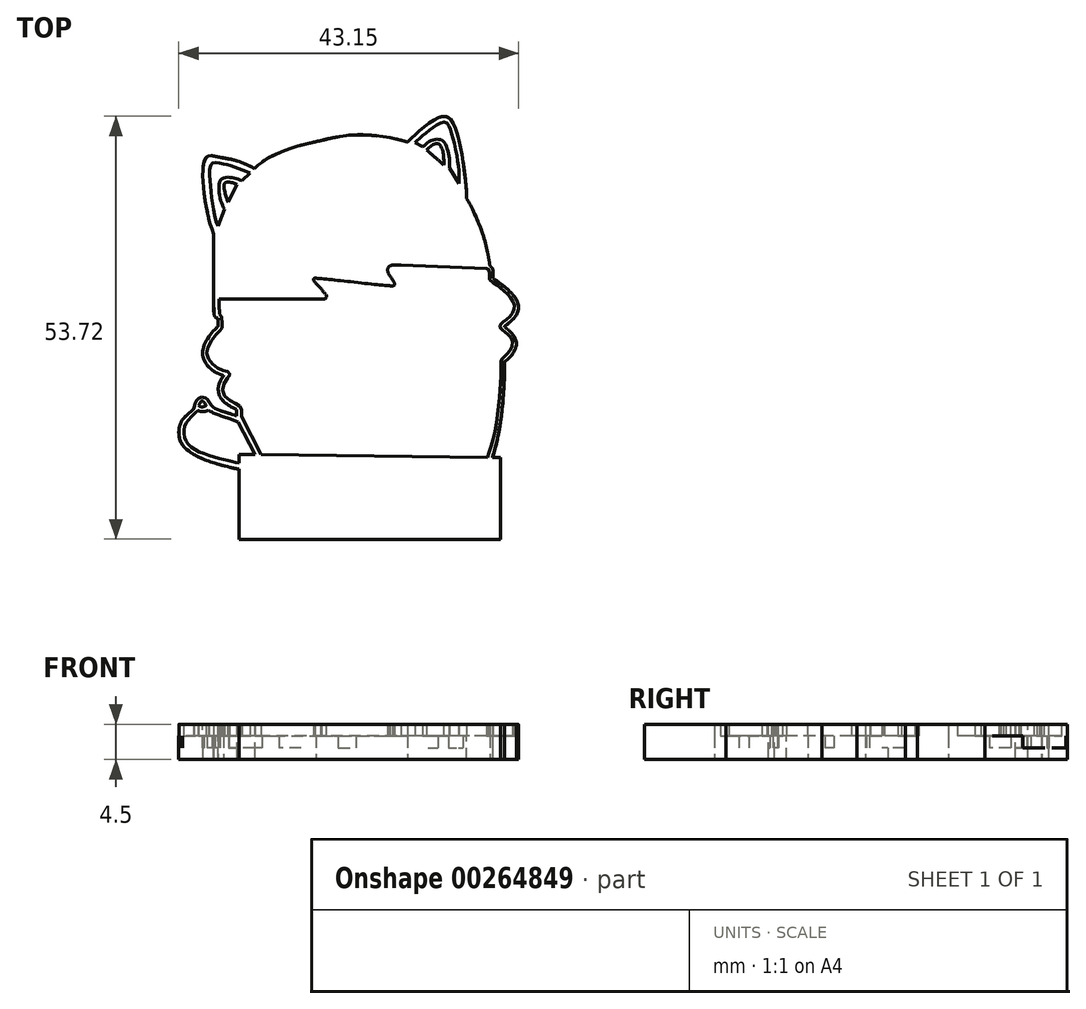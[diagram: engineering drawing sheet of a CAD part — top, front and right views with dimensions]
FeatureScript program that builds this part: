
annotation { "Feature Type Name" : "Feature", "Feature Type Description" : "" }
export const myFeature = defineFeature(function(context is Context, id is Id, definition is map)
    precondition{}
    {
        {
            var Q0;
            Q0=qCreatedBy(makeId("Top.planeOp"),FACE);
            var sketch = newSketch(context, id + "F0", { "sketchPlane" : qUnion([Q0])});
            skFitSpline(sketch, "E0", {"points": [v(-4.71, 21.15) * mm, v(-1.43, 21.85) * mm, v(2.13, 21.99) * mm, v(6.91, 21.1) * mm], "startDerivative": vector(9.73, 2.51) * mm, "endDerivative": vector(9.57, -3.47) * mm});
            skFitSpline(sketch, "E1", {"points": [v(6.91, 21.1) * mm, v(8.61, 22.68) * mm, v(10.2, 23.86) * mm, v(11.92, 24.32) * mm, v(13.1, 22.58) * mm, v(13.82, 19.54) * mm, v(14.44, 13.93) * mm], "startDerivative": vector(10.14, 10.11) * mm, "endDerivative": vector(0.67, -28.32) * mm});
            skFitSpline(sketch, "E2", {"points": [v(14.44, 13.93) * mm, v(15.56, 11.75) * mm, v(16.78, 8.45) * mm, v(17.4, 5.36) * mm], "startDerivative": vector(3.7, -6.8) * mm, "endDerivative": vector(1.45, -8.92) * mm});
            skFitSpline(sketch, "E3", {"points": [v(17.4, 5.36) * mm, v(17.73, 5.01) * mm, v(17.81, 4.5) * mm, v(17.81, 3.8) * mm], "startDerivative": vector(1.74, -1.34) * mm, "endDerivative": vector(0, -1.77) * mm});
            skFitSpline(sketch, "E4", {"points": [v(17.81, 3.8) * mm, v(19.4, 2.59) * mm, v(20.85, 0.9) * mm, v(20.85, -0.67) * mm, v(19.23, -2.33) * mm], "startDerivative": vector(6.54, -4.55) * mm, "endDerivative": vector(-7.42, -5.9) * mm});
            skFitSpline(sketch, "E5", {"points": [v(19.23, -2.33) * mm, v(20.06, -3.07) * mm, v(20.76, -4.46) * mm, v(20.23, -5.87) * mm, v(19.72, -6.4) * mm, v(19.25, -6.8) * mm], "startDerivative": vector(3.94, -3.89) * mm, "endDerivative": vector(-1.7, -1.2) * mm});
            skFitSpline(sketch, "E6", {"points": [v(19.25, -6.8) * mm, v(19.25, -8.45) * mm, v(18.85, -13.72) * mm, v(18.26, -16.97) * mm, v(17.71, -18.96) * mm], "startDerivative": vector(0.22, -7.28) * mm, "endDerivative": vector(-3.1, -9.32) * mm});
            skFitSpline(sketch, "E7", {"points": [v(-4.71, 21.15) * mm, v(-6.69, 20.68) * mm, v(-9.12, 19.83) * mm, v(-11.15, 18.86) * mm, v(-12.47, 17.72) * mm], "startDerivative": vector(-7.9, -1.66) * mm, "endDerivative": vector(-5.4, -5.31) * mm});
            skFitSpline(sketch, "E8", {"points": [v(-12.47, 17.72) * mm, v(-14.84, 18.75) * mm, v(-17.4, 19.25) * mm, v(-18.62, 19.2) * mm, v(-19.07, 16.98) * mm, v(-18.62, 12.76) * mm, v(-17.7, 9.27) * mm], "startDerivative": vector(-13.9, 7.08) * mm, "endDerivative": vector(5.2, -17.3) * mm});
            skFitSpline(sketch, "E9", {"points": [v(-17.7, 9.27) * mm, v(-17.7, 3.92) * mm, v(-17.7, 1.58) * mm], "startDerivative": vector(0, -9.8) * mm, "endDerivative": vector(0, -5.28) * mm});
            skFitSpline(sketch, "E10", {"points": [v(-17.7, 1.58) * mm, v(-17.7, -0.27) * mm, v(-17.48, -1.15) * mm, v(-17.12, -1.27) * mm], "startDerivative": vector(-0.1, -4.19) * mm, "endDerivative": vector(1.9, -0.2) * mm});
            skFitSpline(sketch, "E11", {"points": [v(-17.12, -1.27) * mm, v(-17.12, -2.27) * mm], "startDerivative": vector(0, -1) * mm, "endDerivative": vector(0, -1) * mm});
            skFitSpline(sketch, "E12", {"points": [v(-17.12, -2.27) * mm, v(-17.94, -3.16) * mm, v(-18.85, -4.56) * mm, v(-19, -6.33) * mm, v(-17.77, -7.93) * mm, v(-16.43, -8.56) * mm], "startDerivative": vector(-4.65, -4.51) * mm, "endDerivative": vector(7.01, -2.37) * mm});
            skFitSpline(sketch, "E13", {"points": [v(-16.43, -8.56) * mm, v(-16.98, -9.54) * mm, v(-17.1, -10.55) * mm, v(-16.7, -11.55) * mm, v(-15.79, -12.33) * mm, v(-14.77, -12.9) * mm], "startDerivative": vector(-2.9, -4.58) * mm, "endDerivative": vector(3.19, -2.1) * mm});
            skFitSpline(sketch, "E14", {"points": [v(-14.77, -12.9) * mm, v(-14.77, -13.67) * mm], "startDerivative": vector(0, -0.77) * mm, "endDerivative": vector(0, -0.77) * mm});
            skFitSpline(sketch, "E15", {"points": [v(-14.77, -13.67) * mm, v(-16.26, -13.2) * mm, v(-17.76, -12.58) * mm, v(-18.4, -11.72) * mm, v(-19.08, -11.3) * mm, v(-19.79, -11.63) * mm, v(-20.11, -12.33) * mm, v(-20.24, -12.76) * mm, v(-21.55, -14.05) * mm, v(-22.12, -15.73) * mm, v(-21.73, -17.26) * mm, v(-20.45, -18.43) * mm, v(-18.29, -19.45) * mm, v(-15.98, -20.12) * mm, v(-14.46, -20.43) * mm], "startDerivative": vector(-16.97, 4.2) * mm, "endDerivative": vector(20.47, -2.36) * mm});
            skLineSegment(sketch, "E16", {"start": v(-14.46, -20.43) * mm, "end": v(-14.46, -29.34) * mm});
            skLineSegment(sketch, "E17", {"start": v(-14.46, -29.34) * mm, "end": v(18.77, -29.34) * mm});
            skLineSegment(sketch, "E18", {"start": v(18.77, -29.34) * mm, "end": v(18.77, -18.96) * mm});
            skLineSegment(sketch, "E19", {"start": v(18.77, -18.96) * mm, "end": v(17.71, -18.96) * mm});
            skSolve(sketch);
        }
        {
            var Q0;
            Q0 = qSketchRegion(id + "F0", true);
            extrude(context, id + "F1", {"entities" : qUnion([Q0]), "depth" : 3 * mm, "offsetDistance" : 25 * mm});
        }
        {
            var Q0;
            Q0=makeQuery(id+"F1.opExtrude","CAP_FACE",FACE,{"disambiguationData":[OSD([sQuery(id+"F0.wireOp",EDGE,"E0"),sQuery(id+"F0.wireOp",EDGE,"E1"),sQuery(id+"F0.wireOp",EDGE,"E2"),sQuery(id+"F0.wireOp",EDGE,"E3"),sQuery(id+"F0.wireOp",EDGE,"E4"),sQuery(id+"F0.wireOp",EDGE,"E5"),sQuery(id+"F0.wireOp",EDGE,"E6"),sQuery(id+"F0.wireOp",EDGE,"E7"),sQuery(id+"F0.wireOp",EDGE,"E8"),sQuery(id+"F0.wireOp",EDGE,"E9"),sQuery(id+"F0.wireOp",EDGE,"E10"),sQuery(id+"F0.wireOp",EDGE,"E11"),sQuery(id+"F0.wireOp",EDGE,"E12"),sQuery(id+"F0.wireOp",EDGE,"E13"),sQuery(id+"F0.wireOp",EDGE,"E14"),sQuery(id+"F0.wireOp",EDGE,"E15"),sQuery(id+"F0.wireOp",EDGE,"E16"),sQuery(id+"F0.wireOp",EDGE,"E17"),sQuery(id+"F0.wireOp",EDGE,"E18"),sQuery(id+"F0.wireOp",EDGE,"E19")])],"isStart":false});
            var sketch = newSketch(context, id + "F2", { "sketchPlane" : qUnion([Q0])});
            skFitSpline(sketch, "E20", {"points": [v(6.91, 21.1) * mm, v(8.72, 22.77) * mm, v(10.83, 24.18) * mm, v(12.13, 24.22) * mm, v(13.15, 22.42) * mm, v(13.97, 18.7) * mm, v(14.4, 14.87) * mm, v(14.44, 13.93) * mm], "startDerivative": vector(11.52, 11.3) * mm, "endDerivative": vector(0.21, -7.73) * mm});
            skFitSpline(sketch, "E21", {"points": [v(8.86, 20.52) * mm, v(9.6, 21.1) * mm, v(10.42, 21.43) * mm, v(11.3, 21.33) * mm, v(11.9, 20.45) * mm, v(12.23, 19.04) * mm, v(12.28, 17.78) * mm], "startDerivative": vector(4.55, 4.03) * mm, "endDerivative": vector(0, -6.83) * mm});
            skFitSpline(sketch, "E22", {"points": [v(7.9, 21.02) * mm, v(8.86, 20.52) * mm], "startDerivative": vector(0.97, -0.5) * mm, "endDerivative": vector(0.97, -0.5) * mm});
            skFitSpline(sketch, "E23", {"points": [v(12.28, 17.78) * mm, v(13.45, 15.83) * mm], "startDerivative": vector(1.17, -1.95) * mm, "endDerivative": vector(1.17, -1.95) * mm});
            skFitSpline(sketch, "E24", {"points": [v(13.45, 15.83) * mm, v(13.45, 17.22) * mm, v(13.25, 19.08) * mm, v(12.7, 21.6) * mm, v(12.24, 23) * mm, v(11.72, 23.65) * mm, v(10.6, 23.23) * mm, v(9.43, 22.38) * mm, v(8.37, 21.51) * mm, v(7.9, 21.02) * mm], "startDerivative": vector(0.3, 12.13) * mm, "endDerivative": vector(-5.35, -5.83) * mm});
            skFitSpline(sketch, "E25", {"points": [v(-12.47, 17.72) * mm, v(-11.56, 18.55) * mm, v(-9.36, 19.74) * mm, v(-6.58, 20.7) * mm, v(-4.71, 21.15) * mm, v(-1.9, 21.77) * mm, v(0.4, 22.02) * mm, v(3.08, 21.9) * mm, v(5.35, 21.53) * mm, v(6.91, 21.1) * mm], "startDerivative": vector(9.56, 9.95) * mm, "endDerivative": vector(15.75, -4.57) * mm});
            skFitSpline(sketch, "E26", {"points": [v(-12.47, 17.72) * mm, v(-14.62, 18.68) * mm, v(-17.14, 19.2) * mm, v(-18.54, 19.25) * mm, v(-19.07, 17.21) * mm, v(-18.9, 14.45) * mm, v(-18.33, 11.5) * mm, v(-17.7, 9.27) * mm], "startDerivative": vector(-14.32, 7.5) * mm, "endDerivative": vector(4.5, -14.96) * mm});
            skFitSpline(sketch, "E27", {"points": [v(-13.05, 17.17) * mm, v(-14.39, 17.72) * mm, v(-15.75, 18.16) * mm, v(-16.93, 18.43) * mm, v(-17.95, 18.4) * mm, v(-18.19, 16.74) * mm, v(-17.95, 14.1) * mm, v(-17.48, 11.38) * mm, v(-17.15, 10.44) * mm], "startDerivative": vector(-11.18, 4.71) * mm, "endDerivative": vector(3.4, -8.06) * mm});
            skFitSpline(sketch, "E28", {"points": [v(-17.15, 10.44) * mm, v(-16.34, 12.6) * mm], "startDerivative": vector(0.8, 2.17) * mm, "endDerivative": vector(0.8, 2.17) * mm});
            skFitSpline(sketch, "E29", {"points": [v(-13.05, 17.17) * mm, v(-14.11, 16.23) * mm], "startDerivative": vector(-1.06, -0.95) * mm, "endDerivative": vector(-1.06, -0.95) * mm});
            skFitSpline(sketch, "E30", {"points": [v(-16.34, 12.6) * mm, v(-16.8, 13.69) * mm, v(-17.03, 15.26) * mm, v(-16.77, 16.35) * mm, v(-15.87, 16.64) * mm, v(-14.96, 16.48) * mm, v(-14.11, 16.23) * mm], "startDerivative": vector(-3.12, 5.8) * mm, "endDerivative": vector(5.64, -1.75) * mm});
            skFitSpline(sketch, "E31", {"points": [v(-14.74, 15.7) * mm, v(-15.89, 13.47) * mm], "startDerivative": vector(-1.02, -2) * mm, "endDerivative": vector(-1.02, -2) * mm});
            skFitSpline(sketch, "E32", {"points": [v(-14.74, 15.7) * mm, v(-15.55, 16) * mm, v(-16.3, 15.87) * mm, v(-16.22, 14.55) * mm, v(-15.89, 13.47) * mm], "startDerivative": vector(-2.7, 1.54) * mm, "endDerivative": vector(1.83, -5.13) * mm});
            skFitSpline(sketch, "E33", {"points": [v(9.37, 20.1) * mm, v(11.5, 18.2) * mm], "startDerivative": vector(1.87, -1.81) * mm, "endDerivative": vector(1.87, -1.81) * mm});
            skFitSpline(sketch, "E34", {"points": [v(11.5, 18.2) * mm, v(11.52, 19.2) * mm, v(11.42, 19.89) * mm, v(10.93, 20.85) * mm, v(10.12, 20.74) * mm, v(9.37, 20.1) * mm], "startDerivative": vector(1.24, 3.09) * mm, "endDerivative": vector(-3.44, -3.64) * mm});
            skFitSpline(sketch, "E35", {"points": [v(-17.7, 9.27) * mm, v(-17.7, 3.73) * mm, v(-17.71, 0.83) * mm], "startDerivative": vector(0, -10.33) * mm, "endDerivative": vector(-0.04, -6.35) * mm});
            skFitSpline(sketch, "E36", {"points": [v(-17.71, 0.83) * mm, v(-17.67, -0.6) * mm], "startDerivative": vector(0.04, -1.42) * mm, "endDerivative": vector(0.04, -1.42) * mm});
            skFitSpline(sketch, "E37", {"points": [v(-17.67, -0.6) * mm, v(-17.5, -1.12) * mm, v(-17.12, -1.27) * mm], "startDerivative": vector(0.17, -1.17) * mm, "endDerivative": vector(0.95, -0.17) * mm});
            skFitSpline(sketch, "E38", {"points": [v(-17.01, 1.15) * mm, v(-16.98, 0) * mm, v(-16.95, -0.71) * mm], "startDerivative": vector(0.05, -2.06) * mm, "endDerivative": vector(0.06, -1.5) * mm});
            skFitSpline(sketch, "E39", {"points": [v(-16.95, -0.71) * mm, v(-16.72, -0.96) * mm, v(-16.65, -2.08) * mm, v(-16.66, -2.54) * mm, v(-16.97, -2.91) * mm, v(-17.4, -3.4) * mm, v(-18.34, -4.75) * mm, v(-18.57, -5.8) * mm, v(-18.1, -6.82) * mm, v(-17.12, -7.65) * mm, v(-16.27, -7.99) * mm, v(-15.8, -8.1) * mm, v(-15.62, -8.42) * mm, v(-15.93, -8.88) * mm, v(-16.52, -9.96) * mm, v(-16.3, -11.16) * mm, v(-15.26, -11.94) * mm, v(-14.58, -12.32) * mm, v(-14.2, -12.62) * mm, v(-14.16, -13.76) * mm], "startDerivative": vector(8.18, -4.66) * mm, "endDerivative": vector(-1.08, -25.57) * mm});
            skFitSpline(sketch, "E40", {"points": [v(-17.12, -1.27) * mm, v(-17.12, -2.27) * mm], "startDerivative": vector(0, -1) * mm, "endDerivative": vector(0, -1) * mm});
            skFitSpline(sketch, "E41", {"points": [v(-17.12, -2.27) * mm, v(-18.32, -3.65) * mm, v(-19.06, -5.25) * mm, v(-18.99, -6.4) * mm, v(-18.23, -7.54) * mm, v(-17.25, -8.24) * mm, v(-16.43, -8.56) * mm], "startDerivative": vector(-6.51, -6.68) * mm, "endDerivative": vector(5.98, -2.03) * mm});
            skFitSpline(sketch, "E42", {"points": [v(-16.43, -8.56) * mm, v(-16.8, -9.16) * mm, v(-17.1, -10.14) * mm, v(-16.78, -11.43) * mm, v(-15.79, -12.33) * mm, v(-14.77, -12.9) * mm], "startDerivative": vector(-2.3, -3.21) * mm, "endDerivative": vector(4.9, -2.45) * mm});
            skFitSpline(sketch, "E43", {"points": [v(-14.77, -12.9) * mm, v(-14.77, -13.67) * mm], "startDerivative": vector(0, -0.77) * mm, "endDerivative": vector(0, -0.77) * mm});
            skFitSpline(sketch, "E44", {"points": [v(-14.77, -13.67) * mm, v(-15.72, -13.37) * mm, v(-16.9, -13) * mm, v(-17.87, -12.47) * mm, v(-18.47, -11.62) * mm, v(-19.2, -11.3) * mm, v(-19.96, -11.88) * mm, v(-20.17, -12.61) * mm, v(-20.48, -13.02) * mm, v(-21.44, -13.92) * mm, v(-21.94, -14.73) * mm, v(-22.1, -16.07) * mm, v(-21.66, -17.35) * mm, v(-20.55, -18.37) * mm, v(-19.04, -19.15) * mm, v(-17.44, -19.72) * mm, v(-15.04, -20.34) * mm, v(-14.46, -20.43) * mm], "startDerivative": vector(-16.72, 5.07) * mm, "endDerivative": vector(11.07, -1.55) * mm});
            skFitSpline(sketch, "E45", {"points": [v(-17.01, 1.15) * mm, v(-11.36, 1.15) * mm, v(-5.07, 1.15) * mm, v(-4.09, 1.15) * mm], "startDerivative": vector(12.98, 0.01) * mm, "endDerivative": vector(4.57, -0.03) * mm});
            skFitSpline(sketch, "E46", {"points": [v(-4.84, 3.33) * mm, v(-4.12, 2.55) * mm, v(-3.57, 1.87) * mm, v(-3.35, 1.52) * mm, v(-3.53, 1.2) * mm, v(-4.09, 1.15) * mm], "startDerivative": vector(2.45, -3.14) * mm, "endDerivative": vector(-2.45, -0.3) * mm});
            skFitSpline(sketch, "E47", {"points": [v(-4.84, 3.33) * mm, v(-5.02, 3.6) * mm, v(-4.99, 3.77) * mm, v(-4, 3.75) * mm], "startDerivative": vector(-1.1, 1.36) * mm, "endDerivative": vector(2.68, -0.22) * mm});
            skFitSpline(sketch, "E48", {"points": [v(-4, 3.75) * mm, v(-1.46, 3.49) * mm, v(2.36, 3.08) * mm, v(4.68, 2.85) * mm], "startDerivative": vector(7.49, -0.73) * mm, "endDerivative": vector(7.1, -0.65) * mm});
            skFitSpline(sketch, "E49", {"points": [v(4.68, 2.85) * mm, v(5.21, 2.89) * mm, v(5.29, 3.07) * mm, v(5, 3.65) * mm], "startDerivative": vector(1.05, -0.14) * mm, "endDerivative": vector(-1.14, 1.83) * mm});
            skFitSpline(sketch, "E50", {"points": [v(5, 3.65) * mm, v(4.5, 4.46) * mm, v(4.4, 4.98) * mm, v(4.63, 5.35) * mm], "startDerivative": vector(-1.42, 2) * mm, "endDerivative": vector(1.55, 1.35) * mm});
            skFitSpline(sketch, "E51", {"points": [v(4.63, 5.35) * mm, v(5.04, 5.48) * mm, v(6.08, 5.48) * mm], "startDerivative": vector(1.42, 0.76) * mm, "endDerivative": vector(3.54, -0.11) * mm});
            skLineSegment(sketch, "E52", {"start": v(6.08, 5.48) * mm, "end": v(16.96, 5.03) * mm});
            skFitSpline(sketch, "E53", {"points": [v(16.96, 5.03) * mm, v(17.23, 4.92) * mm, v(17.33, 4.22) * mm, v(17.33, 3.7) * mm, v(17.42, 3.54) * mm, v(17.99, 3.16) * mm, v(19, 2.33) * mm, v(19.87, 1.52) * mm, v(20.45, 0.53) * mm, v(20.43, -0.3) * mm, v(19.8, -1.17) * mm, v(18.97, -1.86) * mm, v(18.7, -2.12) * mm, v(18.65, -2.34) * mm, v(18.87, -2.64) * mm, v(19.32, -3.03) * mm], "startDerivative": vector(6.93, -0.7) * mm, "endDerivative": vector(7.68, -7.42) * mm});
            skFitSpline(sketch, "E54", {"points": [v(14.44, 13.93) * mm, v(15.22, 12.46) * mm, v(16.5, 9.36) * mm, v(17.1, 7.1) * mm, v(17.4, 5.36) * mm], "startDerivative": vector(3.38, -6.02) * mm, "endDerivative": vector(1.25, -7.72) * mm});
            skFitSpline(sketch, "E55", {"points": [v(17.4, 5.36) * mm, v(17.59, 5.2) * mm, v(17.77, 4.9) * mm, v(17.81, 4.12) * mm, v(17.81, 3.8) * mm], "startDerivative": vector(0.96, -0.66) * mm, "endDerivative": vector(0, -1.3) * mm});
            skFitSpline(sketch, "E56", {"points": [v(17.81, 3.8) * mm, v(18.3, 3.45) * mm, v(19.4, 2.58) * mm, v(20.37, 1.63) * mm, v(20.96, 0.6) * mm, v(20.94, -0.46) * mm, v(20.44, -1.26) * mm, v(19.54, -2.09) * mm, v(19.23, -2.33) * mm], "startDerivative": vector(4.43, -3.07) * mm, "endDerivative": vector(-3.32, -2.7) * mm});
            skFitSpline(sketch, "E57", {"points": [v(19.32, -3.03) * mm, v(19.76, -3.43) * mm, v(20.21, -4.03) * mm, v(20.23, -4.83) * mm, v(19.8, -5.55) * mm, v(19.24, -6.14) * mm, v(18.94, -6.43) * mm, v(18.83, -6.68) * mm, v(18.82, -7.23) * mm, v(18.8, -8.34) * mm, v(18.73, -10.04) * mm, v(18.51, -12.45) * mm, v(18.06, -15.47) * mm, v(17.48, -17.75) * mm, v(17.08, -18.96) * mm], "startDerivative": vector(8.1, -7.2) * mm, "endDerivative": vector(-4.92, -14.5) * mm});
            skFitSpline(sketch, "E58", {"points": [v(-14.16, -13.76) * mm, v(-11.65, -18.59) * mm], "startDerivative": vector(2.52, -4.83) * mm, "endDerivative": vector(2.52, -4.83) * mm});
            skFitSpline(sketch, "E59", {"points": [v(-12.44, -18.59) * mm, v(-14.62, -14.42) * mm], "startDerivative": vector(-2.18, 4.16) * mm, "endDerivative": vector(-2.18, 4.16) * mm});
            skFitSpline(sketch, "E60", {"points": [v(-14.62, -14.42) * mm, v(-15.64, -14.03) * mm, v(-17.25, -13.5) * mm, v(-18.22, -13.06) * mm, v(-18.35, -12.95) * mm], "startDerivative": vector(-3.42, 1.4) * mm, "endDerivative": vector(-0.9, 0.86) * mm});
            skFitSpline(sketch, "E61", {"points": [v(-18.35, -12.95) * mm, v(-18.67, -13.08) * mm, v(-19.24, -13.14) * mm, v(-19.7, -12.99) * mm], "startDerivative": vector(-1.04, -0.46) * mm, "endDerivative": vector(-1.5, 0.52) * mm});
            skFitSpline(sketch, "E62", {"points": [v(-19.7, -12.99) * mm, v(-20.37, -13.64) * mm, v(-21.3, -14.82) * mm, v(-21.41, -16.22) * mm, v(-20.66, -17.56) * mm, v(-18.46, -18.64) * mm, v(-15.94, -19.35) * mm, v(-14.46, -19.68) * mm], "startDerivative": vector(-5.77, -5.64) * mm, "endDerivative": vector(10.14, -2.12) * mm});
            skLineSegment(sketch, "E63", {"start": v(-12.44, -18.59) * mm, "end": v(-14.46, -18.59) * mm});
            skFitSpline(sketch, "E64", {"points": [v(-14.46, -18.59) * mm, v(-14.46, -19.68) * mm], "startDerivative": vector(0, -1.1) * mm, "endDerivative": vector(0, -1.1) * mm});
            skLineSegment(sketch, "E65", {"start": v(-11.65, -18.59) * mm, "end": v(17.08, -18.96) * mm});
            skLineSegment(sketch, "E66", {"start": v(17.71, -18.96) * mm, "end": v(18.77, -18.96) * mm});
            skLineSegment(sketch, "E67", {"start": v(18.77, -18.96) * mm, "end": v(18.77, -29.34) * mm});
            skLineSegment(sketch, "E68", {"start": v(18.77, -29.34) * mm, "end": v(-14.46, -29.34) * mm});
            skLineSegment(sketch, "E69", {"start": v(-14.46, -29.34) * mm, "end": v(-14.46, -20.43) * mm});
            skFitSpline(sketch, "E70", {"points": [v(17.71, -18.96) * mm, v(18.07, -17.75) * mm, v(18.7, -14.74) * mm, v(19.2, -9.63) * mm, v(19.25, -6.8) * mm], "startDerivative": vector(2.08, 6.67) * mm, "endDerivative": vector(0.02, 10.4) * mm});
            skFitSpline(sketch, "E71", {"points": [v(19.25, -6.8) * mm, v(20.08, -6.05) * mm, v(20.6, -5.22) * mm, v(20.75, -4.36) * mm, v(20.26, -3.3) * mm, v(19.23, -2.33) * mm], "startDerivative": vector(4.4, 3.61) * mm, "endDerivative": vector(-4.67, 4.12) * mm});
            skFitSpline(sketch, "E72", {"points": [v(-19.6, -12.39) * mm, v(-19.13, -12.54) * mm, v(-18.63, -12.35) * mm], "startDerivative": vector(0.73, -0.42) * mm, "endDerivative": vector(0.97, 0.47) * mm});
            skFitSpline(sketch, "E73", {"points": [v(-18.63, -12.35) * mm, v(-18.98, -11.88) * mm, v(-19.16, -11.77) * mm, v(-19.35, -11.9) * mm, v(-19.6, -12.39) * mm], "startDerivative": vector(-1.22, 1.84) * mm, "endDerivative": vector(-0.77, -1.93) * mm});
            skSolve(sketch);
        }
        {
            var Q0;
            Q0 = qSketchRegion(id + "F2", true);
            extrude(context, id + "F3", {"entities" : qUnion([Q0]), "operationType" : NewBodyOperationType.ADD, "endBound" : BoundingType.SYMMETRIC, "depth" : 3 * mm, "offsetDistance" : 25 * mm});
        }
    });
